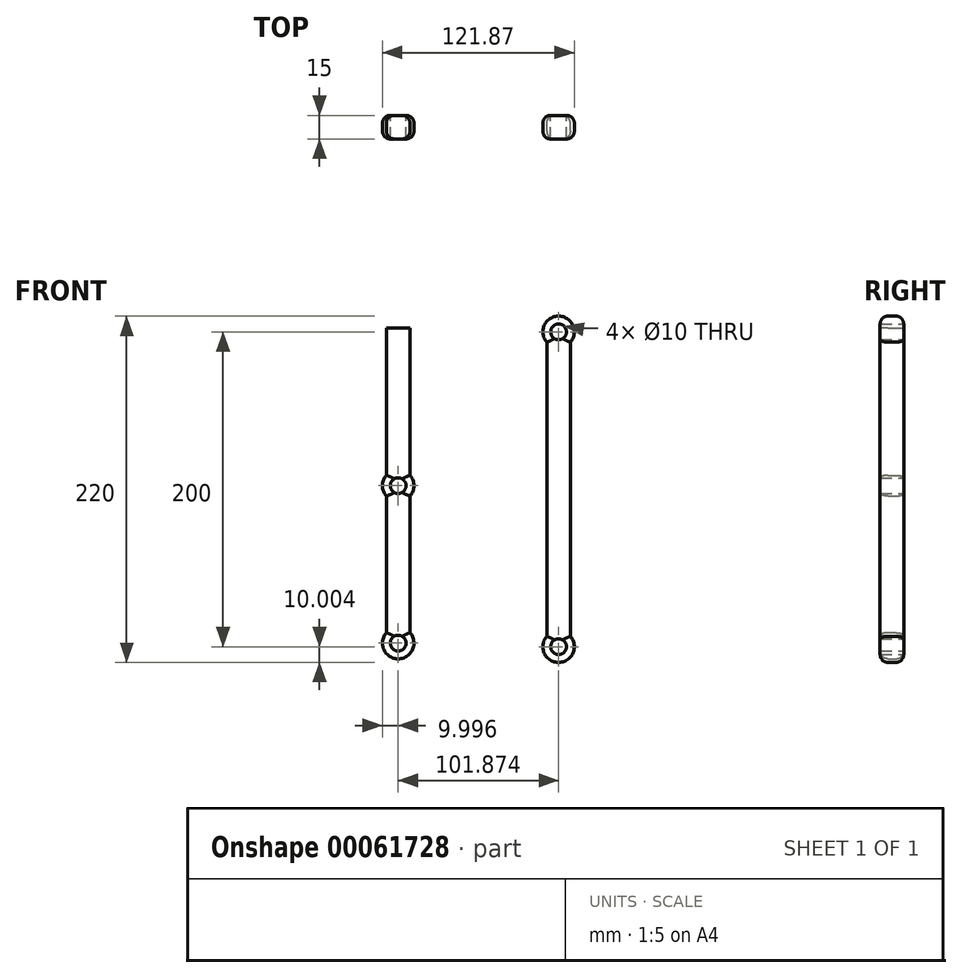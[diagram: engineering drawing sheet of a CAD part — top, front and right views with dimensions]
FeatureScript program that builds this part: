
annotation { "Feature Type Name" : "Feature", "Feature Type Description" : "" }
export const myFeature = defineFeature(function(context is Context, id is Id, definition is map)
    precondition{}
    {
        {
            var Q0;
            Q0=qCreatedBy(makeId("Front.planeOp"),FACE);
            var sketch = newSketch(context, id + "F0", { "sketchPlane" : qUnion([Q0])});
            skCircle(sketch, "E0", {"center": v(0, 186.55) * mm, "radius": 10 * mm});
            skCircle(sketch, "E1", {"center": v(0, 186.55) * mm, "radius": 5 * mm});
            skCircle(sketch, "E2", {"center": v(0, -13.45) * mm, "radius": 10 * mm});
            skCircle(sketch, "E3", {"center": v(0, -13.45) * mm, "radius": 5 * mm});
            skLineSegment(sketch, "E4", {"start": v(-7.5, 179.94) * mm, "end": v(-7.5, -6.83) * mm});
            skLineSegment(sketch, "E5.MirrorCS", {"start": v(7.5, 179.94) * mm, "end": v(7.5, -6.83) * mm});
            skSolve(sketch);
        }
        {
            var Q0;
            {var subQ0=sQuery(id+"F0.wireOp",EDGE,"E4");Q0=makeQuery(id+"F0.imprint","IMPRINT",FACE,{"disambiguationData":[TD([[makeQuery(id+"F0.imprint","IMPRINT",EDGE,{"derivedFrom":subQ0}),1.0]])]});}
            var Q1;
            Q1=makeQuery(id+"F0.imprint","IMPRINT",FACE,{"disambiguationData":[TD([[makeQuery(id+"F0.imprint","IMPRINT",EDGE,{"derivedFrom":sQuery(id+"F0.wireOp",EDGE,"E1")}),-1.0]])]});
            var Q2;
            Q2=makeQuery(id+"F0.imprint","IMPRINT",FACE,{"disambiguationData":[TD([[makeQuery(id+"F0.imprint","IMPRINT",EDGE,{"derivedFrom":sQuery(id+"F0.wireOp",EDGE,"E3")}),-1.0]])]});
            extrude(context, id + "F1", {"entities" : qUnion([Q0, Q1, Q2]), "depth" : 15 * mm});
        }
        {
            var Q0;
            Q0=makeQuery(id+"F1.opExtrude","CAP_EDGE",EDGE,{"disambiguationData":[OSD([sQuery(id+"F0.wireOp",EDGE,"E0")])],"isStart":false});
            var Q1;
            Q1=makeQuery(id+"F1.opExtrude","CAP_EDGE",EDGE,{"disambiguationData":[OSD([sQuery(id+"F0.wireOp",EDGE,"E4")])],"isStart":false});
            var Q2;
            Q2=makeQuery(id+"F1.opExtrude","CAP_EDGE",EDGE,{"disambiguationData":[OSD([sQuery(id+"F0.wireOp",EDGE,"E2")])],"isStart":false});
            var Q3;
            Q3=makeQuery(id+"F1.opExtrude","CAP_EDGE",EDGE,{"disambiguationData":[OSD([sQuery(id+"F0.wireOp",EDGE,"E5.MirrorCS")])],"isStart":false});
            var Q4;
            Q4=makeQuery(id+"F1.opExtrude","CAP_EDGE",EDGE,{"disambiguationData":[OSD([sQuery(id+"F0.wireOp",EDGE,"E4")])],"isStart":true});
            var Q5;
            Q5=makeQuery(id+"F1.opExtrude","CAP_EDGE",EDGE,{"disambiguationData":[OSD([sQuery(id+"F0.wireOp",EDGE,"E0")])],"isStart":true});
            var Q6;
            Q6=makeQuery(id+"F1.opExtrude","CAP_EDGE",EDGE,{"disambiguationData":[OSD([sQuery(id+"F0.wireOp",EDGE,"E5.MirrorCS")])],"isStart":true});
            var Q7;
            Q7=makeQuery(id+"F1.opExtrude","CAP_EDGE",EDGE,{"disambiguationData":[OSD([sQuery(id+"F0.wireOp",EDGE,"E2")])],"isStart":true});
            fillet(context, id + "F2", {"entities" : qUnion([Q0, Q1, Q2, Q3, Q4, Q5, Q6, Q7]), "radius" : 5 * mm, "tangentPropagation" : true, "allowEdgeOverflow" : false});
        }
        {
            var Q0;
            Q0=qCreatedBy(makeId("Front.planeOp"),FACE);
            var sketch = newSketch(context, id + "F3", { "sketchPlane" : qUnion([Q0])});
            skCircle(sketch, "E6", {"center": v(-101.87, 88.85) * mm, "radius": 10 * mm});
            skCircle(sketch, "E7", {"center": v(-101.87, 88.85) * mm, "radius": 5 * mm});
            skCircle(sketch, "E8", {"center": v(-101.87, -11.15) * mm, "radius": 10 * mm});
            skCircle(sketch, "E9", {"center": v(-101.87, -11.15) * mm, "radius": 5 * mm});
            skLineSegment(sketch, "E10", {"start": v(-109.37, 82.23) * mm, "end": v(-109.37, -4.54) * mm});
            skLineSegment(sketch, "E11.MirrorCS", {"start": v(-94.37, 82.23) * mm, "end": v(-94.37, -4.54) * mm});
            skLineSegment(sketch, "E12", {"start": v(-109.37, 95.46) * mm, "end": v(-109.37, 188.85) * mm});
            skLineSegment(sketch, "E13", {"start": v(-109.37, 188.85) * mm, "end": v(-94.37, 188.85) * mm});
            skLineSegment(sketch, "E14", {"start": v(-94.37, 188.85) * mm, "end": v(-94.37, 95.46) * mm});
            skSolve(sketch);
        }
        {
            var Q0;
            Q0=makeQuery(id+"F3.imprint","IMPRINT",FACE,{"disambiguationData":[TD([[makeQuery(id+"F3.imprint","IMPRINT",EDGE,{"derivedFrom":sQuery(id+"F3.wireOp",EDGE,"E7")}),-1.0]])]});
            var Q1;
            Q1=makeQuery(id+"F3.imprint","IMPRINT",FACE,{"disambiguationData":[TD([[makeQuery(id+"F3.imprint","IMPRINT",EDGE,{"derivedFrom":sQuery(id+"F3.wireOp",EDGE,"E9")}),-1.0]])]});
            var Q2;
            {var subQ0=sQuery(id+"F3.wireOp",EDGE,"E10");Q2=makeQuery(id+"F3.imprint","IMPRINT",FACE,{"disambiguationData":[TD([[makeQuery(id+"F3.imprint","IMPRINT",EDGE,{"derivedFrom":subQ0}),1.0]])]});}
            var Q3;
            {var subQ0=sQuery(id+"F3.wireOp",EDGE,"E12");Q3=makeQuery(id+"F3.imprint","IMPRINT",FACE,{"disambiguationData":[TD([[makeQuery(id+"F3.imprint","IMPRINT",EDGE,{"derivedFrom":subQ0}),-1.0]])]});}
            extrude(context, id + "F4", {"entities" : qUnion([Q0, Q1, Q2, Q3]), "depth" : 15 * mm});
        }
        {
            var Q0;
            Q0=makeQuery(id+"F4.opExtrude","CAP_EDGE",EDGE,{"disambiguationData":[OSD([sQuery(id+"F3.wireOp",EDGE,"E10")])],"isStart":false});
            var Q1;
            Q1=makeQuery(id+"F4.opExtrude","CAP_EDGE",EDGE,{"disambiguationData":[OSD([sQuery(id+"F3.wireOp",EDGE,"E11.MirrorCS")])],"isStart":false});
            var Q2;
            {var subQ0=sQuery(id+"F3.wireOp",EDGE,"E6");Q2=makeQuery(id+"F4.opExtrude","CAP_EDGE",EDGE,{"disambiguationData":[OSD([subQ0]),TDD([makeQuery(id+"F3.imprint","IMPRINT",EDGE,{"disambiguationData":[TD([[makeQuery(id+"F3.imprint","INTERSECT",VERTEX,{"derivedFrom":[subQ0,sQuery(id+"F3.wireOp",EDGE,"E11.MirrorCS")]}),-1.0]])],"derivedFrom":subQ0})])],"isStart":false});}
            var Q3;
            {var subQ0=sQuery(id+"F3.wireOp",EDGE,"E6");Q3=makeQuery(id+"F4.opExtrude","CAP_EDGE",EDGE,{"disambiguationData":[OSD([subQ0]),TDD([makeQuery(id+"F3.imprint","IMPRINT",EDGE,{"disambiguationData":[TD([[makeQuery(id+"F3.imprint","INTERSECT",VERTEX,{"derivedFrom":[subQ0,sQuery(id+"F3.wireOp",EDGE,"E10")]}),1.0]])],"derivedFrom":subQ0})])],"isStart":false});}
            var Q4;
            Q4=makeQuery(id+"F4.opExtrude","CAP_EDGE",EDGE,{"disambiguationData":[OSD([sQuery(id+"F3.wireOp",EDGE,"E8")])],"isStart":false});
            var Q5;
            Q5=makeQuery(id+"F4.opExtrude","CAP_EDGE",EDGE,{"disambiguationData":[OSD([sQuery(id+"F3.wireOp",EDGE,"E12")])],"isStart":false});
            var Q6;
            Q6=makeQuery(id+"F4.opExtrude","CAP_EDGE",EDGE,{"disambiguationData":[OSD([sQuery(id+"F3.wireOp",EDGE,"E14")])],"isStart":false});
            var Q7;
            Q7=makeQuery(id+"F4.opExtrude","CAP_EDGE",EDGE,{"disambiguationData":[OSD([sQuery(id+"F3.wireOp",EDGE,"E8")])],"isStart":true});
            var Q8;
            Q8=makeQuery(id+"F4.opExtrude","CAP_EDGE",EDGE,{"disambiguationData":[OSD([sQuery(id+"F3.wireOp",EDGE,"E10")])],"isStart":true});
            var Q9;
            Q9=makeQuery(id+"F4.opExtrude","CAP_EDGE",EDGE,{"disambiguationData":[OSD([sQuery(id+"F3.wireOp",EDGE,"E11.MirrorCS")])],"isStart":true});
            var Q10;
            {var subQ0=sQuery(id+"F3.wireOp",EDGE,"E6");Q10=makeQuery(id+"F4.opExtrude","CAP_EDGE",EDGE,{"disambiguationData":[OSD([subQ0]),TDD([makeQuery(id+"F3.imprint","IMPRINT",EDGE,{"disambiguationData":[TD([[makeQuery(id+"F3.imprint","INTERSECT",VERTEX,{"derivedFrom":[subQ0,sQuery(id+"F3.wireOp",EDGE,"E10")]}),1.0]])],"derivedFrom":subQ0})])],"isStart":true});}
            var Q11;
            {var subQ0=sQuery(id+"F3.wireOp",EDGE,"E6");Q11=makeQuery(id+"F4.opExtrude","CAP_EDGE",EDGE,{"disambiguationData":[OSD([subQ0]),TDD([makeQuery(id+"F3.imprint","IMPRINT",EDGE,{"disambiguationData":[TD([[makeQuery(id+"F3.imprint","INTERSECT",VERTEX,{"derivedFrom":[subQ0,sQuery(id+"F3.wireOp",EDGE,"E11.MirrorCS")]}),-1.0]])],"derivedFrom":subQ0})])],"isStart":true});}
            var Q12;
            Q12=makeQuery(id+"F4.opExtrude","CAP_EDGE",EDGE,{"disambiguationData":[OSD([sQuery(id+"F3.wireOp",EDGE,"E12")])],"isStart":true});
            var Q13;
            Q13=makeQuery(id+"F4.opExtrude","CAP_EDGE",EDGE,{"disambiguationData":[OSD([sQuery(id+"F3.wireOp",EDGE,"E14")])],"isStart":true});
            fillet(context, id + "F5", {"entities" : qUnion([Q0, Q1, Q2, Q3, Q4, Q5, Q6, Q7, Q8, Q9, Q10, Q11, Q12, Q13]), "radius" : 5 * mm, "tangentPropagation" : true, "allowEdgeOverflow" : false});
        }
    });
